# Revit family: Hager-GOLF-Surface_mounted-IP40-With_Cover-With_DIN-NoHosted-ES-es
name_source: partatom
category: Electrical Equipment
units: mm (PartAtom-declared; Revit-internal decimal feet)

## family parameters
Always vertical = Yes
Cut with Voids When Loaded = No
Maintain Annotation Orientation = No
Panel Configuration = Two Columns, Circuits Across
Part Type = Panelboard
Room Calculation Point = No
Round Connector Dimension = Use Diameter
Shared = No
Work Plane-Based = Yes

## types (38) — shared parameters
Code hager = ADD-EC000214_EU
Default Elevation = 1200 mm
EF000003 - Método de montaje = Montado superficial (escayola)
EF000007 - Color = Blanco
EF000024 - Resistente a UV = No
EF000049 - Profundidad = 99 mm  [stored 0.324803 ft]
EF000116 - Número RAL = 9010
EF000118 - Con placa de montaje = No
EF001062 - Versión de CEM = No
EF001088 - Posibilidad de extensión = Yes
EF001134 - Carril DIN = Yes
EF004462 - Tipo de cierre = Otros
EF005474 - Grado de protección (IP) = IP40
EF006306 - Con candado = No
EF009212 - Versión de la cubierta = Cerrado
EF015941 - Puerta de transmisión de señal = Yes
ETIM class code = EC000214
ETIM class name = Small distribution board
HG000001 - Número de columnas = 1
HG000002-with door or cover-es = Yes
HG000003-Range-es = GOLF
HG000005-Thickness-es = 2 mm  [stored 0.00656168 ft]
HG000006-Flush mounted-es = No
HG000009-Double swing door-es = No
HG000010-Asymmetric doors-es = No
HG000011-Empty rows from bottom-es = No
HG000012-Door swing angle-es = 90.00°
HG000013-Door on the left-es = No
HG000014-Door on the right-es = Yes
HG000015-Clearance visibility-es = Yes
HG000016-Door 3D visibility-es = Yes
HG000017-Distance between poles-es = 18 mm  [stored 0.0590551 ft]
HG000060-RAL-number = 9010
HG000099-Onfly Template ID-es-ES = 507532
Manufacturer = Hager
Name BIM&CO = Electricity
Name hager = ADD_Enclosures_EC000214
Reference = Template-Enclosure_EU-EC000214
Uniformat = Low Tension Service & Dist.
Uniformat code = D501001
zero-valued in all types: EF000218 - Profundidad de instalación, EF000332 - Altura de la instalación, EF000846 - Anchura de montaje, EF001131 - Profundidad interna, HG000007-Number of empty columns-es, HG000008-Number of empty rows-es

## per-type parameters (varying)
| type | BC_METADATA | EF000008 - Anchura | EF000040 - Altura | EF000266 - Número de filas | EF002950 - Ancho en número de espacios modulares | EF006244 - Tapa/puerta transparente | EF015776 - Borne de tierra | EF015777 - Borne neutro | HG000004-Manufacturer reference-es | HGEF000266-Número de filas | HGEF0002950-Ancho en número de espacios modulares |
| GOLF-Surface_mounted_W138_H184_D99_4_Modular_Spacing-VS104PE | {"ObjectGuid":"307a4dc4-d2f8-4903-bb55-8e5842d951ec","ModelGuid":"71160acc-142d-4b3a-8590-45dc452b7c8d","VariantGuid":"79b509d4-39a9-4cb8-a066-ac2a99bd9554","Revision":"#5","VariantName":"GOLF-Surface_mounted_W138_H184_D99_4_Modular_Spacing-VS104PE"} | 138 mm  [stored 0.452756 ft] | 184 mm  [stored 0.603675 ft] | 1 | 4 | No | Yes | No | VS104PE | 1 | 4 |
| GOLF-Surface_mounted_W138_H184_D99_4_Modular_Spacing-VS104PEB | {"ObjectGuid":"307a4dc4-d2f8-4903-bb55-8e5842d951ec","ModelGuid":"71160acc-142d-4b3a-8590-45dc452b7c8d","VariantGuid":"fc443a78-20d2-4b6c-8fbe-83721a51f329","Revision":"#5","VariantName":"GOLF-Surface_mounted_W138_H184_D99_4_Modular_Spacing-VS104PEB"} | 138 mm  [stored 0.452756 ft] | 184 mm  [stored 0.603675 ft] | 1 | 4 | No | No | No | VS104PEB | 1 | 4 |
| GOLF-Surface_mounted_W138_H184_D99_4_Modular_Spacing-VS104TE | {"ObjectGuid":"307a4dc4-d2f8-4903-bb55-8e5842d951ec","ModelGuid":"71160acc-142d-4b3a-8590-45dc452b7c8d","VariantGuid":"4c9afcd8-27c2-43e1-97c8-76a06714a298","Revision":"#5","VariantName":"GOLF-Surface_mounted_W138_H184_D99_4_Modular_Spacing-VS104TE"} | 138 mm  [stored 0.452756 ft] | 184 mm  [stored 0.603675 ft] | 1 | 4 | Yes | Yes | No | VS104TE | 1 | 4 |
| GOLF-Surface_mounted_W210_H184_D99_8_Modular_Spacing-VS108PE | {"ObjectGuid":"307a4dc4-d2f8-4903-bb55-8e5842d951ec","ModelGuid":"71160acc-142d-4b3a-8590-45dc452b7c8d","VariantGuid":"ce0b9fa5-b7ab-420e-9121-3e4d85af3ec6","Revision":"#5","VariantName":"GOLF-Surface_mounted_W210_H184_D99_8_Modular_Spacing-VS108PE"} | 210 mm  [stored 0.688976 ft] | 184 mm  [stored 0.603675 ft] | 1 | 8 | No | Yes | No | VS108PE | 1 | 8 |
| GOLF-Surface_mounted_W210_H184_D99_8_Modular_Spacing-VS108PEB | {"ObjectGuid":"307a4dc4-d2f8-4903-bb55-8e5842d951ec","ModelGuid":"71160acc-142d-4b3a-8590-45dc452b7c8d","VariantGuid":"36c3adbe-de88-42d0-80d7-0b013d78d0a2","Revision":"#5","VariantName":"GOLF-Surface_mounted_W210_H184_D99_8_Modular_Spacing-VS108PEB"} | 210 mm  [stored 0.688976 ft] | 184 mm  [stored 0.603675 ft] | 1 | 8 | No | No | No | VS108PEB | 1 | 8 |
| GOLF-Surface_mounted_W210_H184_D99_8_Modular_Spacing-VS108TE | {"ObjectGuid":"307a4dc4-d2f8-4903-bb55-8e5842d951ec","ModelGuid":"71160acc-142d-4b3a-8590-45dc452b7c8d","VariantGuid":"570812b1-fc5e-4f35-ac82-db78e10ec6f9","Revision":"#5","VariantName":"GOLF-Surface_mounted_W210_H184_D99_8_Modular_Spacing-VS108TE"} | 210 mm  [stored 0.688976 ft] | 184 mm  [stored 0.603675 ft] | 1 | 8 | Yes | Yes | No | VS108TE | 1 | 8 |
| GOLF-Surface_mounted_W282_H252_D99_12_Modular_Spacing-VS112PE | {"ObjectGuid":"307a4dc4-d2f8-4903-bb55-8e5842d951ec","ModelGuid":"71160acc-142d-4b3a-8590-45dc452b7c8d","VariantGuid":"62a24093-d709-41ab-b2e7-dfb1c4cdb7bd","Revision":"#5","VariantName":"GOLF-Surface_mounted_W282_H252_D99_12_Modular_Spacing-VS112PE"} | 282 mm | 252 mm  [stored 0.826772 ft] | 1 | 12 | No | Yes | No | VS112PE | 1 | 12 |
| GOLF-Surface_mounted_W282_H252_D99_12_Modular_Spacing-VS112PEB | {"ObjectGuid":"307a4dc4-d2f8-4903-bb55-8e5842d951ec","ModelGuid":"71160acc-142d-4b3a-8590-45dc452b7c8d","VariantGuid":"a0fc1ccd-8843-4c77-9997-acc060c2dc63","Revision":"#5","VariantName":"GOLF-Surface_mounted_W282_H252_D99_12_Modular_Spacing-VS112PEB"} | 282 mm | 252 mm  [stored 0.826772 ft] | 1 | 12 | No | No | No | VS112PEB | 1 | 12 |
| GOLF-Surface_mounted_W282_H252_D99_12_Modular_Spacing-VS112PY | {"ObjectGuid":"307a4dc4-d2f8-4903-bb55-8e5842d951ec","ModelGuid":"71160acc-142d-4b3a-8590-45dc452b7c8d","VariantGuid":"4ca2825e-fc60-418b-91af-07c57e7c0719","Revision":"#5","VariantName":"GOLF-Surface_mounted_W282_H252_D99_12_Modular_Spacing-VS112PY"} | 282 mm | 252 mm  [stored 0.826772 ft] | 1 | 12 | No | Yes | Yes | VS112PY | 1 | 12 |
| GOLF-Surface_mounted_W282_H252_D99_12_Modular_Spacing-VS112TE | {"ObjectGuid":"307a4dc4-d2f8-4903-bb55-8e5842d951ec","ModelGuid":"71160acc-142d-4b3a-8590-45dc452b7c8d","VariantGuid":"824f9d56-b3c5-4020-892f-d56036a2a183","Revision":"#5","VariantName":"GOLF-Surface_mounted_W282_H252_D99_12_Modular_Spacing-VS112TE"} | 282 mm | 252 mm  [stored 0.826772 ft] | 1 | 12 | Yes | Yes | No | VS112TE | 1 | 12 |
| GOLF-Surface_mounted_W390_H252_D99_18_Modular_Spacing-VS118PES | {"ObjectGuid":"307a4dc4-d2f8-4903-bb55-8e5842d951ec","ModelGuid":"71160acc-142d-4b3a-8590-45dc452b7c8d","VariantGuid":"4a6272d8-432a-410a-aea8-48e4aaf67c31","Revision":"#5","VariantName":"GOLF-Surface_mounted_W390_H252_D99_18_Modular_Spacing-VS118PES"} | 390 mm  [stored 1.27953 ft] | 252 mm  [stored 0.826772 ft] | 1 | 18 | No | No | No | VS118PES | 1 | 18 |
| GOLF-Surface_mounted_W390_H252_D99_18_Modular_Spacing-VS118PY | {"ObjectGuid":"307a4dc4-d2f8-4903-bb55-8e5842d951ec","ModelGuid":"71160acc-142d-4b3a-8590-45dc452b7c8d","VariantGuid":"4fe1a263-436d-4855-9e93-f1c3cb409719","Revision":"#5","VariantName":"GOLF-Surface_mounted_W390_H252_D99_18_Modular_Spacing-VS118PY"} | 390 mm  [stored 1.27953 ft] | 252 mm  [stored 0.826772 ft] | 1 | 18 | No | Yes | Yes | VS118PY | 1 | 18 |
| GOLF-Surface_mounted_W390_H252_D99_18_Modular_Spacing-VS118TES | {"ObjectGuid":"307a4dc4-d2f8-4903-bb55-8e5842d951ec","ModelGuid":"71160acc-142d-4b3a-8590-45dc452b7c8d","VariantGuid":"bb105955-7f27-40da-89cc-4e24387a1968","Revision":"#5","VariantName":"GOLF-Surface_mounted_W390_H252_D99_18_Modular_Spacing-VS118TES"} | 390 mm  [stored 1.27953 ft] | 252 mm  [stored 0.826772 ft] | 1 | 18 | Yes | No | No | VS118TES | 1 | 18 |
| GOLF-Surface_mounted_W390_H252_D99_18_Modular_Spacing-VS118TF | {"ObjectGuid":"307a4dc4-d2f8-4903-bb55-8e5842d951ec","ModelGuid":"71160acc-142d-4b3a-8590-45dc452b7c8d","VariantGuid":"6b72334b-061d-4689-80b0-aa4bdcbe36fd","Revision":"#5","VariantName":"GOLF-Surface_mounted_W390_H252_D99_18_Modular_Spacing-VS118TF"} | 390 mm  [stored 1.27953 ft] | 252 mm  [stored 0.826772 ft] | 1 | 18 | Yes | Yes | No | VS118TF | 1 | 18 |
| GOLF-Surface_mounted_W462_H252_D99_22_Modular_Spacing-VS122PY | {"ObjectGuid":"307a4dc4-d2f8-4903-bb55-8e5842d951ec","ModelGuid":"71160acc-142d-4b3a-8590-45dc452b7c8d","VariantGuid":"eb61cd08-0f7d-47a7-aa88-c3182182eeab","Revision":"#5","VariantName":"GOLF-Surface_mounted_W462_H252_D99_22_Modular_Spacing-VS122PY"} | 462 mm  [stored 1.51575 ft] | 252 mm  [stored 0.826772 ft] | 1 | 22 | No | Yes | Yes | VS122PY | 1 | 22 |
| GOLF-Surface_mounted_W282_H377_D99_12_Modular_Spacing-VS212PE | {"ObjectGuid":"307a4dc4-d2f8-4903-bb55-8e5842d951ec","ModelGuid":"71160acc-142d-4b3a-8590-45dc452b7c8d","VariantGuid":"e748b2e8-b796-41e6-9314-5974cebd3a9b","Revision":"#5","VariantName":"GOLF-Surface_mounted_W282_H377_D99_12_Modular_Spacing-VS212PE"} | 282 mm | 377 mm  [stored 1.23688 ft] | 2 | 12 | No | Yes | No | VS212PE | 2 | 12 |
| GOLF-Surface_mounted_W282_H377_D99_12_Modular_Spacing-VS212PEB | {"ObjectGuid":"307a4dc4-d2f8-4903-bb55-8e5842d951ec","ModelGuid":"71160acc-142d-4b3a-8590-45dc452b7c8d","VariantGuid":"9d41af9a-c5bc-4b01-b071-2b89b057ed0b","Revision":"#5","VariantName":"GOLF-Surface_mounted_W282_H377_D99_12_Modular_Spacing-VS212PEB"} | 282 mm | 377 mm  [stored 1.23688 ft] | 2 | 12 | No | No | No | VS212PEB | 2 | 12 |
| GOLF-Surface_mounted_W282_H377_D99_12_Modular_Spacing-VS212PY | {"ObjectGuid":"307a4dc4-d2f8-4903-bb55-8e5842d951ec","ModelGuid":"71160acc-142d-4b3a-8590-45dc452b7c8d","VariantGuid":"2e222777-93be-44f7-840e-5ac1ceb61b3b","Revision":"#5","VariantName":"GOLF-Surface_mounted_W282_H377_D99_12_Modular_Spacing-VS212PY"} | 282 mm | 377 mm  [stored 1.23688 ft] | 2 | 12 | No | Yes | Yes | VS212PY | 2 | 12 |
| GOLF-Surface_mounted_W282_H377_D99_12_Modular_Spacing-VS212TE | {"ObjectGuid":"307a4dc4-d2f8-4903-bb55-8e5842d951ec","ModelGuid":"71160acc-142d-4b3a-8590-45dc452b7c8d","VariantGuid":"614a19ff-ad76-4ded-8efd-7584ff1da3e2","Revision":"#5","VariantName":"GOLF-Surface_mounted_W282_H377_D99_12_Modular_Spacing-VS212TE"} | 282 mm | 377 mm  [stored 1.23688 ft] | 2 | 12 | Yes | Yes | No | VS212TE | 2 | 12 |
| GOLF-Surface_mounted_W282_H377_D99_12_Modular_Spacing-VS212TY | {"ObjectGuid":"307a4dc4-d2f8-4903-bb55-8e5842d951ec","ModelGuid":"71160acc-142d-4b3a-8590-45dc452b7c8d","VariantGuid":"a896a985-738e-4a9d-a2e1-9b47a3a1d6fa","Revision":"#5","VariantName":"GOLF-Surface_mounted_W282_H377_D99_12_Modular_Spacing-VS212TY"} | 282 mm | 377 mm  [stored 1.23688 ft] | 2 | 12 | Yes | Yes | Yes | VS212TY | 2 | 12 |
| GOLF-Surface_mounted_W390_H377_D99_18_Modular_Spacing-VS218PES | {"ObjectGuid":"307a4dc4-d2f8-4903-bb55-8e5842d951ec","ModelGuid":"71160acc-142d-4b3a-8590-45dc452b7c8d","VariantGuid":"4c3c62e1-e3ba-4242-ab54-d21740f537cf","Revision":"#5","VariantName":"GOLF-Surface_mounted_W390_H377_D99_18_Modular_Spacing-VS218PES"} | 390 mm  [stored 1.27953 ft] | 377 mm  [stored 1.23688 ft] | 2 | 18 | No | No | No | VS218PES | 2 | 18 |
| GOLF-Surface_mounted_W390_H377_D99_18_Modular_Spacing-VS218PY | {"ObjectGuid":"307a4dc4-d2f8-4903-bb55-8e5842d951ec","ModelGuid":"71160acc-142d-4b3a-8590-45dc452b7c8d","VariantGuid":"6ea2146f-a94f-45bd-83a8-f0e2c4cdaf21","Revision":"#5","VariantName":"GOLF-Surface_mounted_W390_H377_D99_18_Modular_Spacing-VS218PY"} | 390 mm  [stored 1.27953 ft] | 377 mm  [stored 1.23688 ft] | 2 | 18 | No | Yes | Yes | VS218PY | 2 | 18 |
| GOLF-Surface_mounted_W390_H377_D99_18_Modular_Spacing-VS218TES | {"ObjectGuid":"307a4dc4-d2f8-4903-bb55-8e5842d951ec","ModelGuid":"71160acc-142d-4b3a-8590-45dc452b7c8d","VariantGuid":"6af14fb9-271a-415b-bf76-f81c11961bb1","Revision":"#5","VariantName":"GOLF-Surface_mounted_W390_H377_D99_18_Modular_Spacing-VS218TES"} | 390 mm  [stored 1.27953 ft] | 377 mm  [stored 1.23688 ft] | 2 | 18 | Yes | No | No | VS218TES | 2 | 18 |
| GOLF-Surface_mounted_W390_H377_D99_18_Modular_Spacing-VS218TY | {"ObjectGuid":"307a4dc4-d2f8-4903-bb55-8e5842d951ec","ModelGuid":"71160acc-142d-4b3a-8590-45dc452b7c8d","VariantGuid":"d1327587-b20a-4fff-98f3-826a3d1f7263","Revision":"#5","VariantName":"GOLF-Surface_mounted_W390_H377_D99_18_Modular_Spacing-VS218TY"} | 390 mm  [stored 1.27953 ft] | 377 mm  [stored 1.23688 ft] | 2 | 18 | Yes | Yes | Yes | VS218TY | 2 | 18 |
| GOLF-Surface_mounted_W282_H500_D99_12_Modular_Spacing-VS312PE | {"ObjectGuid":"307a4dc4-d2f8-4903-bb55-8e5842d951ec","ModelGuid":"71160acc-142d-4b3a-8590-45dc452b7c8d","VariantGuid":"ff9a3b03-1048-4b5f-9d58-b2461085fb6d","Revision":"#5","VariantName":"GOLF-Surface_mounted_W282_H500_D99_12_Modular_Spacing-VS312PE"} | 282 mm | 500 mm  [stored 1.64042 ft] | 3 | 12 | No | Yes | No | VS312PE | 3 | 12 |
| GOLF-Surface_mounted_W282_H500_D99_12_Modular_Spacing-VS312PY | {"ObjectGuid":"307a4dc4-d2f8-4903-bb55-8e5842d951ec","ModelGuid":"71160acc-142d-4b3a-8590-45dc452b7c8d","VariantGuid":"5b1deb81-893f-486b-a394-941ec9b5f3d0","Revision":"#5","VariantName":"GOLF-Surface_mounted_W282_H500_D99_12_Modular_Spacing-VS312PY"} | 282 mm | 500 mm  [stored 1.64042 ft] | 3 | 12 | No | Yes | Yes | VS312PY | 3 | 12 |
| GOLF-Surface_mounted_W282_H500_D99_12_Modular_Spacing-VS312TE | {"ObjectGuid":"307a4dc4-d2f8-4903-bb55-8e5842d951ec","ModelGuid":"71160acc-142d-4b3a-8590-45dc452b7c8d","VariantGuid":"f49f2541-18e1-4e4b-9776-d7b5039663fc","Revision":"#5","VariantName":"GOLF-Surface_mounted_W282_H500_D99_12_Modular_Spacing-VS312TE"} | 282 mm | 500 mm  [stored 1.64042 ft] | 3 | 12 | Yes | Yes | No | VS312TE | 3 | 12 |
| GOLF-Surface_mounted_W390_H500_D99_18_Modular_Spacing-VS318PES | {"ObjectGuid":"307a4dc4-d2f8-4903-bb55-8e5842d951ec","ModelGuid":"71160acc-142d-4b3a-8590-45dc452b7c8d","VariantGuid":"0ac074d4-9fe2-405a-9111-904672f9a3d3","Revision":"#5","VariantName":"GOLF-Surface_mounted_W390_H500_D99_18_Modular_Spacing-VS318PES"} | 390 mm  [stored 1.27953 ft] | 500 mm  [stored 1.64042 ft] | 3 | 18 | No | No | No | VS318PES | 3 | 18 |
| GOLF-Surface_mounted_W390_H500_D99_18_Modular_Spacing-VS318PY | {"ObjectGuid":"307a4dc4-d2f8-4903-bb55-8e5842d951ec","ModelGuid":"71160acc-142d-4b3a-8590-45dc452b7c8d","VariantGuid":"86bdacb4-a047-48e4-88b4-73cc41df2d58","Revision":"#5","VariantName":"GOLF-Surface_mounted_W390_H500_D99_18_Modular_Spacing-VS318PY"} | 390 mm  [stored 1.27953 ft] | 500 mm  [stored 1.64042 ft] | 3 | 18 | No | Yes | Yes | VS318PY | 3 | 18 |
| GOLF-Surface_mounted_W390_H500_D99_18_Modular_Spacing-VS318TES | {"ObjectGuid":"307a4dc4-d2f8-4903-bb55-8e5842d951ec","ModelGuid":"71160acc-142d-4b3a-8590-45dc452b7c8d","VariantGuid":"a687f332-9e62-4673-95e7-95182f81c8fb","Revision":"#5","VariantName":"GOLF-Surface_mounted_W390_H500_D99_18_Modular_Spacing-VS318TES"} | 390 mm  [stored 1.27953 ft] | 500 mm  [stored 1.64042 ft] | 3 | 18 | Yes | No | No | VS318TES | 3 | 18 |
| GOLF-Surface_mounted_W282_H647_D99_12_Modular_Spacing-VS412PE | {"ObjectGuid":"307a4dc4-d2f8-4903-bb55-8e5842d951ec","ModelGuid":"71160acc-142d-4b3a-8590-45dc452b7c8d","VariantGuid":"1a37a3fb-b6f6-4cc6-b4da-c980c2c6fea0","Revision":"#5","VariantName":"GOLF-Surface_mounted_W282_H647_D99_12_Modular_Spacing-VS412PE"} | 282 mm | 647 mm  [stored 2.1227 ft] | 4 | 12 | No | Yes | No | VS412PE | 4 | 12 |
| GOLF-Surface_mounted_W282_H647_D99_12_Modular_Spacing-VS412PY | {"ObjectGuid":"307a4dc4-d2f8-4903-bb55-8e5842d951ec","ModelGuid":"71160acc-142d-4b3a-8590-45dc452b7c8d","VariantGuid":"407457bb-c1c7-41db-b4db-73bc5cf678e5","Revision":"#5","VariantName":"GOLF-Surface_mounted_W282_H647_D99_12_Modular_Spacing-VS412PY"} | 282 mm | 647 mm  [stored 2.1227 ft] | 4 | 12 | No | Yes | Yes | VS412PY | 4 | 12 |
| GOLF-Surface_mounted_W282_H647_D99_12_Modular_Spacing-VS412TE | {"ObjectGuid":"307a4dc4-d2f8-4903-bb55-8e5842d951ec","ModelGuid":"71160acc-142d-4b3a-8590-45dc452b7c8d","VariantGuid":"d6a7d6d9-caf8-4287-8af1-594642825fe6","Revision":"#5","VariantName":"GOLF-Surface_mounted_W282_H647_D99_12_Modular_Spacing-VS412TE"} | 282 mm | 647 mm  [stored 2.1227 ft] | 4 | 12 | Yes | Yes | No | VS412TE | 4 | 12 |
| GOLF-Surface_mounted_W390_H647_D99_18_Modular_Spacing-VS418PES | {"ObjectGuid":"307a4dc4-d2f8-4903-bb55-8e5842d951ec","ModelGuid":"71160acc-142d-4b3a-8590-45dc452b7c8d","VariantGuid":"66f6ae5d-17f0-4df5-8ff3-67f32a90451e","Revision":"#5","VariantName":"GOLF-Surface_mounted_W390_H647_D99_18_Modular_Spacing-VS418PES"} | 390 mm  [stored 1.27953 ft] | 647 mm  [stored 2.1227 ft] | 4 | 18 | No | No | No | VS418PES | 4 | 18 |
| GOLF-Surface_mounted_W390_H647_D99_18_Modular_Spacing-VS418PF | {"ObjectGuid":"307a4dc4-d2f8-4903-bb55-8e5842d951ec","ModelGuid":"71160acc-142d-4b3a-8590-45dc452b7c8d","VariantGuid":"73b2ee7d-2f9d-46e3-bdab-5fe377029b5d","Revision":"#5","VariantName":"GOLF-Surface_mounted_W390_H647_D99_18_Modular_Spacing-VS418PF"} | 390 mm  [stored 1.27953 ft] | 647 mm  [stored 2.1227 ft] | 4 | 18 | No | Yes | No | VS418PF | 4 | 18 |
| GOLF-Surface_mounted_W390_H647_D99_18_Modular_Spacing-VS418PY | {"ObjectGuid":"307a4dc4-d2f8-4903-bb55-8e5842d951ec","ModelGuid":"71160acc-142d-4b3a-8590-45dc452b7c8d","VariantGuid":"75a2dbd1-bcab-4a55-ba73-095e781bba8c","Revision":"#5","VariantName":"GOLF-Surface_mounted_W390_H647_D99_18_Modular_Spacing-VS418PY"} | 390 mm  [stored 1.27953 ft] | 647 mm  [stored 2.1227 ft] | 4 | 18 | No | Yes | Yes | VS418PY | 4 | 18 |
| GOLF-Surface_mounted_W390_H647_D99_18_Modular_Spacing-VS418TES | {"ObjectGuid":"307a4dc4-d2f8-4903-bb55-8e5842d951ec","ModelGuid":"71160acc-142d-4b3a-8590-45dc452b7c8d","VariantGuid":"bb12da88-8ac9-4927-a05c-c237fba0f11d","Revision":"#5","VariantName":"GOLF-Surface_mounted_W390_H647_D99_18_Modular_Spacing-VS418TES"} | 390 mm  [stored 1.27953 ft] | 647 mm  [stored 2.1227 ft] | 4 | 18 | Yes | No | No | VS418TES | 4 | 18 |
| GOLF-Surface_mounted_W390_H647_D99_18_Modular_Spacing-VS418TY | {"ObjectGuid":"307a4dc4-d2f8-4903-bb55-8e5842d951ec","ModelGuid":"71160acc-142d-4b3a-8590-45dc452b7c8d","VariantGuid":"30a008b2-bcb1-496d-bf87-44a79e6387ff","Revision":"#5","VariantName":"GOLF-Surface_mounted_W390_H647_D99_18_Modular_Spacing-VS418TY"} | 390 mm  [stored 1.27953 ft] | 647 mm  [stored 2.1227 ft] | 4 | 18 | Yes | Yes | Yes | VS418TY | 4 | 18 |

note: [stored X ft] marks values corroborated as IEEE doubles in the binary element streams (Revit-internal decimal feet)

## geometry (parser evidence)
native form markers: Sweep x14
no freeform markers — native parametric forms only
